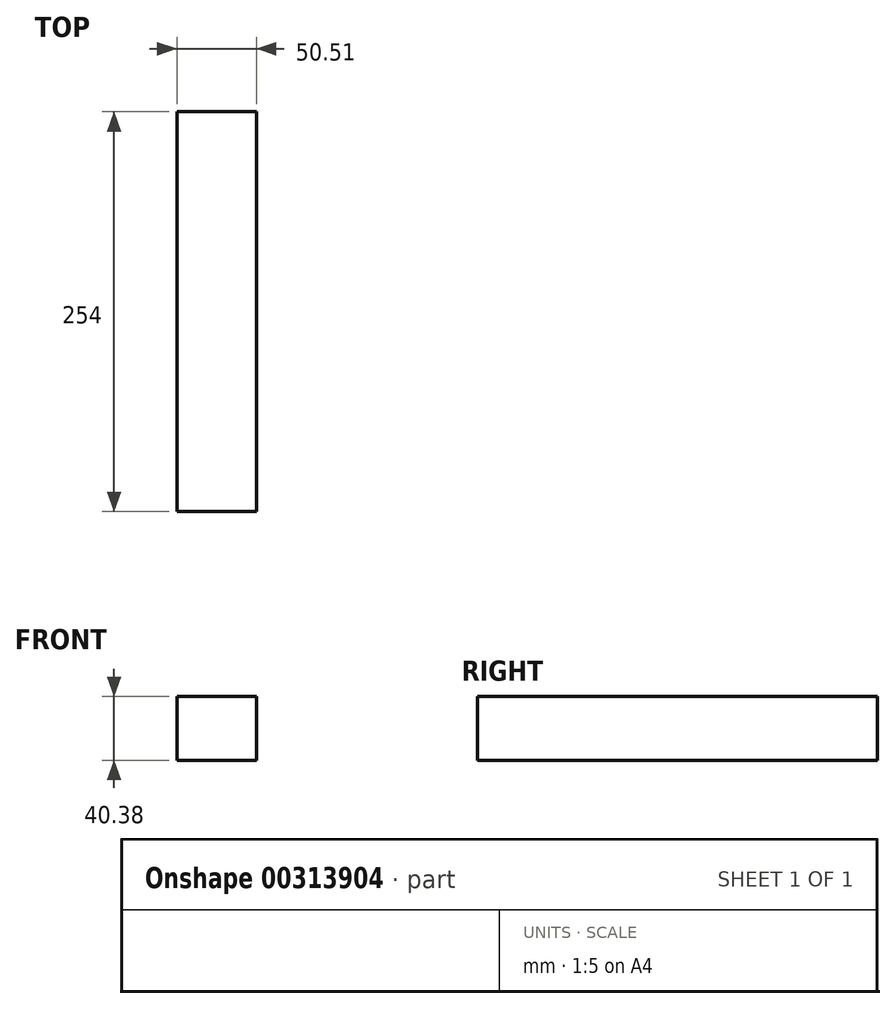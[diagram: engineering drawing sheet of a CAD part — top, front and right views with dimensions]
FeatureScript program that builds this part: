
annotation { "Feature Type Name" : "Feature", "Feature Type Description" : "" }
export const myFeature = defineFeature(function(context is Context, id is Id, definition is map)
    precondition{}
    {
        {
            var Q0;
            Q0=qCreatedBy(makeId("Front.planeOp"),FACE);
            var sketch = newSketch(context, id + "F0", { "sketchPlane" : qUnion([Q0])});
            skLineSegment(sketch, "E0.bottom", {"start": v(-17.51, -4.06) * mm, "end": v(33, -4.06) * mm});
            skLineSegment(sketch, "E0.top", {"start": v(-17.51, 36.32) * mm, "end": v(33, 36.32) * mm});
            skLineSegment(sketch, "E0.left", {"start": v(-17.51, -4.06) * mm, "end": v(-17.51, 36.32) * mm});
            skLineSegment(sketch, "E0.right", {"start": v(33, -4.06) * mm, "end": v(33, 36.32) * mm});
            skSolve(sketch);
        }
        {
            var Q0;
            Q0=makeQuery(id+"F0.imprint","IMPRINT",FACE,{"disambiguationData":[TD([[makeQuery(id+"F0.imprint","IMPRINT",EDGE,{"derivedFrom":sQuery(id+"F0.wireOp",EDGE,"E0.bottom")}),1.0]])]});
            extrude(context, id + "F1", {"entities" : qUnion([Q0]), "depth" : 254 * mm});
        }
    });
